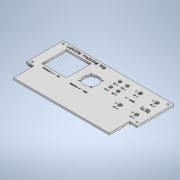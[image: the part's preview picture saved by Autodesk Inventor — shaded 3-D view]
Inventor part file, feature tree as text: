
AUTODESK INVENTOR PART (.ipt)
format: ipt  version: 2022 (Build 260153000, 153)  size: 2,116,096 bytes
history: native  units: in
note: dims shown in document units (in); Inventor stores cm internally (conversion verified against a paired STEP export)
features: sketch x5, extrude x4
ambient origin geometry x8: Origin, YZ Plane, XZ Plane, XY Plane, X Axis, Y Axis, Z Axis, Center Point
bodies: Solid1 (feature_tree)
feature tree (9):
  extrude  "Extrusion1"  Depth=2.1654in
  extrude  "Extrusion2"  Depth=0.7874in
  extrude  "Extrusion3"  Depth=5.9055in
  extrude  "Extrusion4"  Depth=0.1969in TaperAngle=0.0deg
  sketch  "Sketch2"  dims[d2=11.811in d3=0.7874in]
  sketch  "Sketch1"  dims[d0=3.937in d1=2.1654in]
  sketch  "Sketch3"  dims[d4=0.7874in d5=5.9055in]
  sketch  "Sketch4"  dims[d6=1.9685in d7=0.1969in d8=0.0in]
  sketch  "Sketch5"  dims[d11=2.6378in d12=2.6378in d13=0.6496in d15=0.9843in d16=1.5354in d17=1.5748in d18=1.5748in d19=1.2598in d20=1.2598in d23=0.6299in d24=0.6299in d25=0.1181in d26=0.1181in d27=0.1181in d28=0.1181in d29=0.374in d30=1.7717in d31=2.1654in d32=0.7874in d34=0.315in d36=0.7874in d37=0.9843in d38=0.7874in d39=1.6535in d40=1.378in d41=0.4331in d42=0.1024in d43=0.0512in d44=0.1024in d45=0.0512in d46=0.1024in d47=0.0512in d48=0.1024in d49=0.0512in d50=0.4331in d51=0.0in d52=0.0in d55=0.1772in d58=0.315in d59=0.315in d60=0.315in d62=0.315in d63=0.3937in d64=0.0in d65=0.6496in d66=0.3937in d67=0.3937in d68=0.1969in d69=0.1969in d70=0.3937in d71=0.2362in d72=0.2362in d73=0.3937in d74=1.063in d75=0.4331in d76=0.4331in d77=0.4331in d79=0.4331in d80=0.3937in d81=0.3937in d82=0.9055in d83=0.9055in d84=0.1575in d85=0.3937in d86=0.0in]
